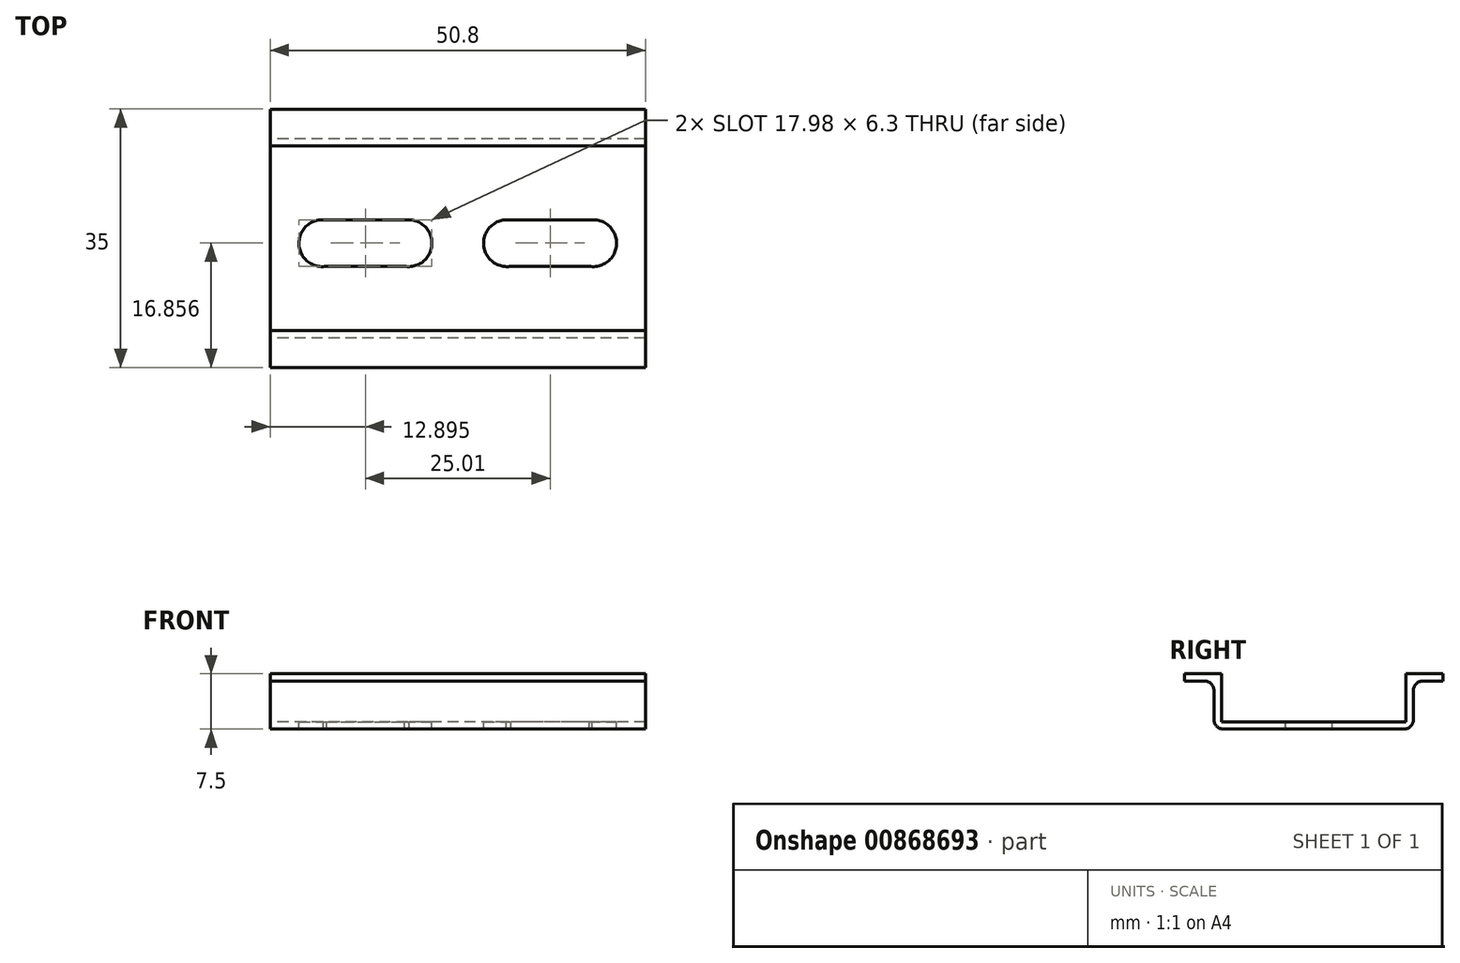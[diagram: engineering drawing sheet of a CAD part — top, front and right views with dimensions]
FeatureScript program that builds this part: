
annotation { "Feature Type Name" : "Feature", "Feature Type Description" : "" }
export const myFeature = defineFeature(function(context is Context, id is Id, definition is map)
    precondition{}
    {
        {
            var Q0;
            Q0=qCreatedBy(makeId("Right.planeOp"),FACE);
            var sketch = newSketch(context, id + "F0", { "sketchPlane" : qUnion([Q0])});
            skLineSegment(sketch, "E0", {"start": v(-18.9, 4.88) * mm, "end": v(-13.9, 4.88) * mm});
            skLineSegment(sketch, "E1", {"start": v(-13.9, 4.88) * mm, "end": v(-13.9, -1.62) * mm});
            skLineSegment(sketch, "E2", {"start": v(-13.9, -1.62) * mm, "end": v(11.1, -1.62) * mm});
            skLineSegment(sketch, "E3", {"start": v(11.1, -1.62) * mm, "end": v(11.1, 4.88) * mm});
            skLineSegment(sketch, "E4", {"start": v(11.1, 4.88) * mm, "end": v(16.1, 4.88) * mm});
            skLineSegment(sketch, "E5", {"start": v(-18.9, 4.88) * mm, "end": v(-18.9, 3.88) * mm});
            skLineSegment(sketch, "E6", {"start": v(-18.9, 3.88) * mm, "end": v(-16.16, 3.88) * mm});
            skLineSegment(sketch, "E7", {"start": v(-14.9, 2.61) * mm, "end": v(-14.9, -1.35) * mm});
            skLineSegment(sketch, "E8", {"start": v(-13.62, -2.62) * mm, "end": v(10.84, -2.62) * mm});
            skLineSegment(sketch, "E9", {"start": v(12.1, -1.35) * mm, "end": v(12.1, 2.61) * mm});
            skLineSegment(sketch, "E10", {"start": v(13.38, 3.88) * mm, "end": v(16.1, 3.88) * mm});
            skLineSegment(sketch, "E11", {"start": v(16.1, 3.88) * mm, "end": v(16.1, 4.88) * mm});
            skPoint(sketch, "E12.visualSharp", {"position": v(-14.9, -2.62) * mm});
            skArc(sketch, "E12.filletArc", {"start": v(-14.9, -1.35) * mm, "mid": v(-14.52, -2.25) * mm, "end": v(-13.62, -2.62) * mm});
            skPoint(sketch, "E13.visualSharp", {"position": v(-14.9, 3.88) * mm});
            skArc(sketch, "E13.filletArc", {"start": v(-14.9, 2.61) * mm, "mid": v(-15.27, 3.51) * mm, "end": v(-16.16, 3.88) * mm});
            skPoint(sketch, "E14.visualSharp", {"position": v(12.1, -2.62) * mm});
            skArc(sketch, "E14.filletArc", {"start": v(10.84, -2.62) * mm, "mid": v(11.73, -2.25) * mm, "end": v(12.1, -1.35) * mm});
            skPoint(sketch, "E15.visualSharp", {"position": v(12.1, 3.88) * mm});
            skArc(sketch, "E15.filletArc", {"start": v(13.38, 3.88) * mm, "mid": v(12.48, 3.51) * mm, "end": v(12.1, 2.61) * mm});
            skSolve(sketch);
        }
        {
            var Q0;
            Q0=makeQuery(id+"F0.imprint","IMPRINT",FACE,{"disambiguationData":[TD([[makeQuery(id+"F0.imprint","IMPRINT",EDGE,{"derivedFrom":sQuery(id+"F0.wireOp",EDGE,"E0")}),-1.0]])]});
            extrude(context, id + "F1", {"entities" : qUnion([Q0]), "endBound" : BoundingType.SYMMETRIC, "depth" : 50.8 * mm, "offsetDistance" : 25.4 * mm});
        }
        {
            var Q0;
            Q0=makeQuery(id+"F1.opExtrude","SWEPT_FACE",FACE,{"disambiguationData":[OSD([sQuery(id+"F0.wireOp",EDGE,"E2")])]});
            var sketch = newSketch(context, id + "F2", { "sketchPlane" : qUnion([Q0])});
            skLineSegment(sketch, "E16", {"start": v(-18.18, 1.12) * mm, "end": v(-6.6, 1.12) * mm});
            skLineSegment(sketch, "E17", {"start": v(-17.78, -5.18) * mm, "end": v(-7.23, -5.18) * mm});
            skArc(sketch, "E18", {"start": v(-7.23, -5.18) * mm, "mid": v(-3.52, -2.38) * mm, "end": v(-6.6, 1.12) * mm});
            skArc(sketch, "E19", {"start": v(-18.18, 1.12) * mm, "mid": v(-21.5, -2.26) * mm, "end": v(-17.78, -5.18) * mm});
            skLineSegment(sketch, "E20", {"start": v(0, 6.39) * mm, "end": v(0, -10.03) * mm});
            skPoint(sketch, "E20.startSnap0", {"position": v(0, 11.1) * mm});
            skArc(sketch, "E21.MirrorCS", {"start": v(18.18, 1.12) * mm, "mid": v(21.5, -2.26) * mm, "end": v(17.78, -5.18) * mm});
            skLineSegment(sketch, "E22.MirrorCS", {"start": v(17.78, -5.18) * mm, "end": v(7.23, -5.18) * mm});
            skLineSegment(sketch, "E23.MirrorCS", {"start": v(18.18, 1.12) * mm, "end": v(6.6, 1.12) * mm});
            skArc(sketch, "E24.MirrorCS", {"start": v(7.23, -5.18) * mm, "mid": v(3.52, -2.38) * mm, "end": v(6.6, 1.12) * mm});
            skSolve(sketch);
        }
        {
            var Q0;
            Q0 = qSketchRegion(id + "F2", true);
            extrude(context, id + "F3", {"entities" : qUnion([Q0]), "operationType" : NewBodyOperationType.REMOVE, "oppositeDirection" : true, "depth" : 25.4 * mm, "offsetDistance" : 25.4 * mm});
        }
    });
